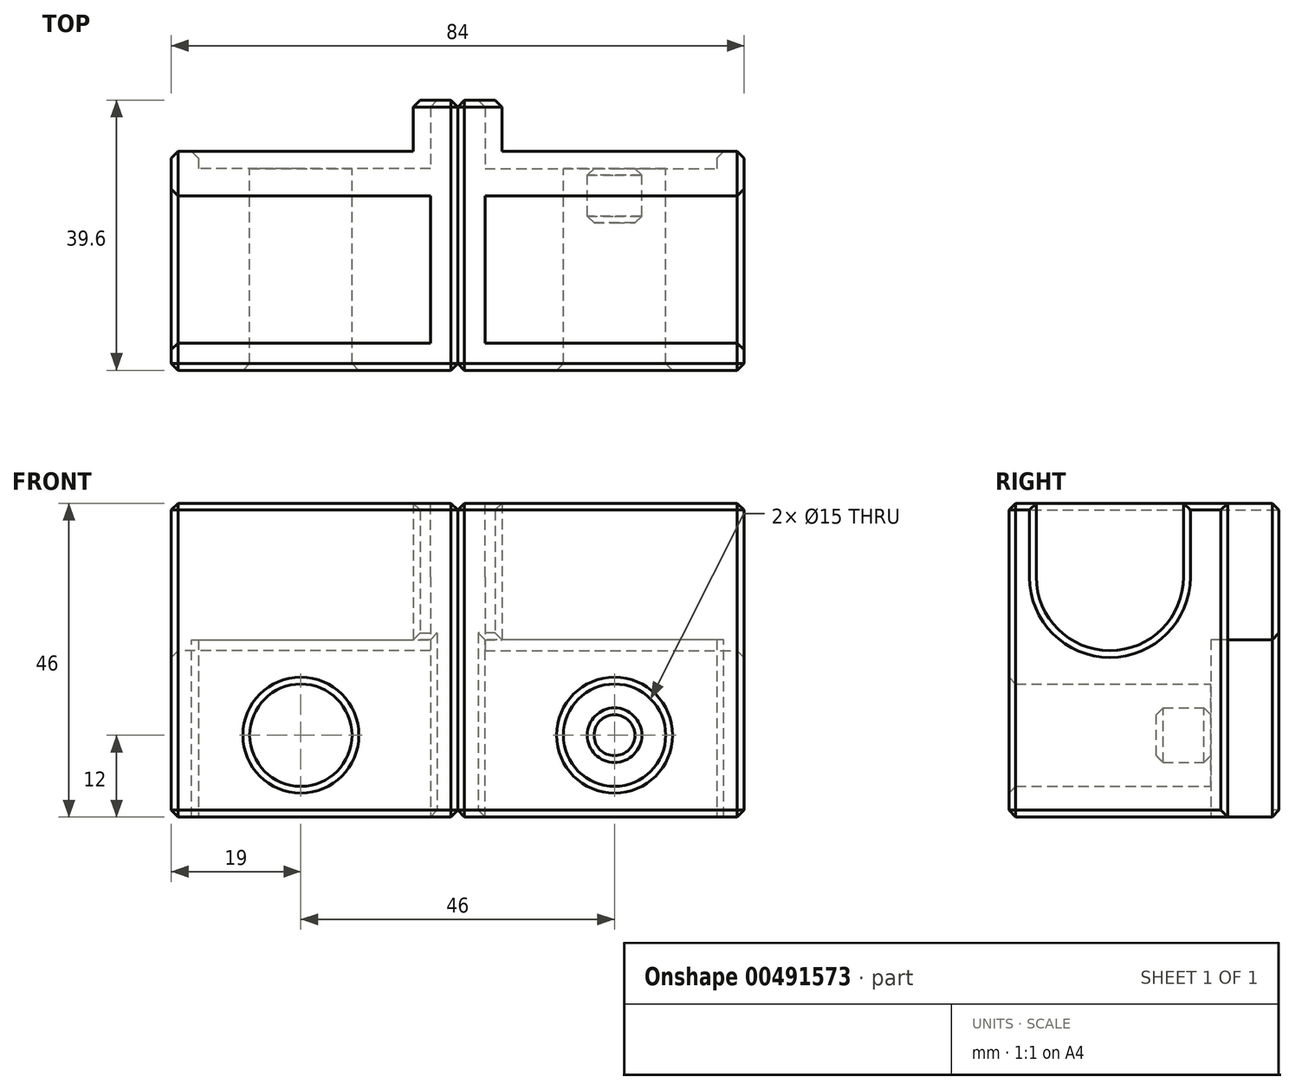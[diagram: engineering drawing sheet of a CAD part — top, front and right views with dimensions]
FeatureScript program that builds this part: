
annotation { "Feature Type Name" : "Feature", "Feature Type Description" : "" }
export const myFeature = defineFeature(function(context is Context, id is Id, definition is map)
    precondition{}
    {
        {
            assignVariable(context, id + "F0", {"name" : "majorEdge", "anyValue" : 19});
        }
        {
            assignVariable(context, id + "F1", {"name" : "minorEdge", "anyValue" : 15});
        }
        {
            assignVariable(context, id + "F2", {"name" : "thickness", "anyValue" : 4});
        }
        {
            assignVariable(context, id + "F3", {"name" : "axleOD", "anyValue" : 21.6});
        }
        {
            assignVariable(context, id + "F4", {"name" : "majorLipDepth", "anyValue" : 10});
        }
        {
            assignVariable(context, id + "F5", {"name" : "minorLipDepth", "anyValue" : 2.5});
        }
        {
            var Q0;
            Q0=qCreatedBy(makeId("Front.planeOp"),FACE);
            var sketch = newSketch(context, id + "F6", { "sketchPlane" : qUnion([Q0])});
            skCircle(sketch, "E0", {"center": v(0, 0) * mm, "radius": 4 * mm});
            skLineSegment(sketch, "E1", {"start": v(0, 4) * mm, "end": v(0, 8) * mm, "construction": true});
            skLineSegment(sketch, "E2", {"start": v(0, 8) * mm, "end": v(-19, 8) * mm});
            skLineSegment(sketch, "E3", {"start": v(-19, 8) * mm, "end": v(-23, 8) * mm});
            skLineSegment(sketch, "E4", {"start": v(0, 8) * mm, "end": v(15, 8) * mm});
            skLineSegment(sketch, "E5", {"start": v(15, 8) * mm, "end": v(19, 8) * mm});
            skLineSegment(sketch, "E6", {"start": v(0, 0) * mm, "end": v(0, -13) * mm, "construction": true});
            skLineSegment(sketch, "E7", {"start": v(0, -13) * mm, "end": v(19, -13) * mm, "construction": true});
            skCircle(sketch, "E8.MirrorC", {"center": v(0, -26) * mm, "radius": 4 * mm});
            skLineSegment(sketch, "E9.MirrorCS", {"start": v(0, -34) * mm, "end": v(15, -34) * mm});
            skLineSegment(sketch, "E10.MirrorCS", {"start": v(0, -34) * mm, "end": v(-19, -34) * mm});
            skLineSegment(sketch, "E11.MirrorCS", {"start": v(-19, -34) * mm, "end": v(-23, -34) * mm});
            skLineSegment(sketch, "E12.MirrorCS", {"start": v(15, -34) * mm, "end": v(19, -34) * mm});
            skLineSegment(sketch, "E13", {"start": v(-23, 8) * mm, "end": v(-23, -34) * mm});
            skLineSegment(sketch, "E14", {"start": v(-19, 8) * mm, "end": v(-19, -34) * mm});
            skLineSegment(sketch, "E15", {"start": v(15, 8) * mm, "end": v(15, -34) * mm});
            skLineSegment(sketch, "E16", {"start": v(19, 8) * mm, "end": v(19, -34) * mm});
            skLineSegment(sketch, "E17", {"start": v(0, -26) * mm, "end": v(0, -12) * mm, "construction": true});
            skLineSegment(sketch, "E18", {"start": v(0, -12) * mm, "end": v(15, -12) * mm});
            skPoint(sketch, "E18.endSnap0", {"position": v(15, -13) * mm});
            skLineSegment(sketch, "E19", {"start": v(0, -12) * mm, "end": v(-19, -12) * mm});
            skCircle(sketch, "E20", {"center": v(0, -26) * mm, "radius": 7.5 * mm});
            skLineSegment(sketch, "E21", {"start": v(-23, -34) * mm, "end": v(-23, -38) * mm});
            skLineSegment(sketch, "E22", {"start": v(-23, -38) * mm, "end": v(19, -38) * mm});
            skLineSegment(sketch, "E23", {"start": v(19, -38) * mm, "end": v(19, -34) * mm});
            skLineSegment(sketch, "E24", {"start": v(15, -34) * mm, "end": v(15, -38) * mm});
            skLineSegment(sketch, "E25", {"start": v(-19, -34) * mm, "end": v(-19, -38) * mm});
            skSolve(sketch);
        }
        {
            var Q0;
            Q0=makeQuery(id+"F6.imprint","IMPRINT",FACE,{"disambiguationData":[TD([[makeQuery(id+"F6.imprint","IMPRINT",EDGE,{"derivedFrom":sQuery(id+"F6.wireOp",EDGE,"E0")}),-1.0]])]});
            var Q1;
            Q1=makeQuery(id+"F6.imprint","IMPRINT",FACE,{"disambiguationData":[TD([[makeQuery(id+"F6.imprint","IMPRINT",EDGE,{"derivedFrom":sQuery(id+"F6.wireOp",EDGE,"E3")}),1.0]])]});
            var Q2;
            Q2=makeQuery(id+"F6.imprint","IMPRINT",FACE,{"disambiguationData":[TD([[makeQuery(id+"F6.imprint","IMPRINT",EDGE,{"derivedFrom":sQuery(id+"F6.wireOp",EDGE,"E5")}),-1.0]])]});
            var Q3;
            Q3=makeQuery(id+"F6.imprint","IMPRINT",FACE,{"disambiguationData":[TD([[makeQuery(id+"F6.imprint","IMPRINT",EDGE,{"derivedFrom":sQuery(id+"F6.wireOp",EDGE,"E0")}),1.0]])]});
            var Q4;
            Q4=makeQuery(id+"F6.imprint","IMPRINT",FACE,{"disambiguationData":[TD([[makeQuery(id+"F6.imprint","IMPRINT",EDGE,{"derivedFrom":sQuery(id+"F6.wireOp",EDGE,"E8.MirrorC")}),1.0]])]});
            var Q5;
            {var subQ1=sQuery(id+"F6.wireOp",EDGE,"E9.MirrorCS");Q5=makeQuery(id+"F6.imprint","IMPRINT",FACE,{"disambiguationData":[TD([[makeQuery(id+"F6.imprint","IMPRINT",EDGE,{"derivedFrom":subQ1}),1.0]])]});}
            var Q6;
            Q6=makeQuery(id+"F6.imprint","IMPRINT",FACE,{"disambiguationData":[TD([[makeQuery(id+"F6.imprint","IMPRINT",EDGE,{"derivedFrom":sQuery(id+"F6.wireOp",EDGE,"E9.MirrorCS")}),-1.0]])]});
            var Q7;
            Q7=makeQuery(id+"F6.imprint","IMPRINT",FACE,{"disambiguationData":[TD([[makeQuery(id+"F6.imprint","IMPRINT",EDGE,{"derivedFrom":sQuery(id+"F6.wireOp",EDGE,"E11.MirrorCS")}),1.0]])]});
            var Q8;
            Q8=makeQuery(id+"F6.imprint","IMPRINT",FACE,{"disambiguationData":[TD([[makeQuery(id+"F6.imprint","IMPRINT",EDGE,{"derivedFrom":sQuery(id+"F6.wireOp",EDGE,"E12.MirrorCS")}),-1.0]])]});
            extrude(context, id + "F7", {"entities" : qUnion([Q0, Q1, Q2, Q3, Q4, Q5, Q6, Q7, Q8]), "depth" : (getVariable(context, 'axleOD') + getVariable(context, 'thickness') * 2) * mm, "offsetDistance" : 25 * mm});
        }
        {
            var Q0;
            Q0=makeQuery(id+"F6.imprint","IMPRINT",FACE,{"disambiguationData":[TD([[makeQuery(id+"F6.imprint","IMPRINT",EDGE,{"derivedFrom":sQuery(id+"F6.wireOp",EDGE,"E0")}),-1.0]])]});
            var Q1;
            Q1=makeQuery(id+"F6.imprint","IMPRINT",FACE,{"disambiguationData":[TD([[makeQuery(id+"F6.imprint","IMPRINT",EDGE,{"derivedFrom":sQuery(id+"F6.wireOp",EDGE,"E0")}),1.0]])]});
            extrude(context, id + "F8", {"entities" : qUnion([Q0, Q1]), "operationType" : NewBodyOperationType.ADD, "oppositeDirection" : true, "depth" : (getVariable(context, 'minorLipDepth')) * mm, "offsetDistance" : 25 * mm});
        }
        {
            var Q0;
            Q0=makeQuery(id+"F6.imprint","IMPRINT",FACE,{"disambiguationData":[TD([[makeQuery(id+"F6.imprint","IMPRINT",EDGE,{"derivedFrom":sQuery(id+"F6.wireOp",EDGE,"E3")}),1.0]])]});
            var Q1;
            Q1=makeQuery(id+"F6.imprint","IMPRINT",FACE,{"disambiguationData":[TD([[makeQuery(id+"F6.imprint","IMPRINT",EDGE,{"derivedFrom":sQuery(id+"F6.wireOp",EDGE,"E11.MirrorCS")}),1.0]])]});
            extrude(context, id + "F9", {"entities" : qUnion([Q0, Q1]), "operationType" : NewBodyOperationType.ADD, "oppositeDirection" : true, "depth" : (getVariable(context, 'majorLipDepth')) * mm, "offsetDistance" : 25 * mm});
        }
        {
            var Q0;
            Q0=makeQuery(id+"F6.imprint","IMPRINT",FACE,{"disambiguationData":[TD([[makeQuery(id+"F6.imprint","IMPRINT",EDGE,{"derivedFrom":sQuery(id+"F6.wireOp",EDGE,"E5")}),-1.0]])]});
            var Q1;
            Q1=makeQuery(id+"F6.imprint","IMPRINT",FACE,{"disambiguationData":[TD([[makeQuery(id+"F6.imprint","IMPRINT",EDGE,{"derivedFrom":sQuery(id+"F6.wireOp",EDGE,"E12.MirrorCS")}),-1.0]])]});
            extrude(context, id + "F10", {"entities" : qUnion([Q0, Q1]), "oppositeDirection" : true, "depth" : (getVariable(context, 'minorLipDepth')) * mm, "offsetDistance" : 25 * mm});
        }
        {
            var Q0;
            Q0=makeQuery(id+"F7.opExtrude","SWEPT_FACE",FACE,{"disambiguationData":[OSD([sQuery(id+"F6.wireOp",EDGE,"E16")])]});
            var sketch = newSketch(context, id + "F11", { "sketchPlane" : qUnion([Q0])});
            skLineSegment(sketch, "E26.0", {"start": v(-29.6, 8) * mm, "end": v(0, 8) * mm, "construction": true});
            skLineSegment(sketch, "E27", {"start": v(-14.8, 8) * mm, "end": v(-14.8, -2.8) * mm, "construction": true});
            skArc(sketch, "E28", {"start": v(-25.6, -2.8) * mm, "mid": v(-14.8, -13.6) * mm, "end": v(-4, -2.8) * mm});
            skLineSegment(sketch, "E29", {"start": v(-25.6, -2.8) * mm, "end": v(-25.6, 8) * mm});
            skLineSegment(sketch, "E30", {"start": v(-4, -2.8) * mm, "end": v(-4, 8) * mm});
            skSolve(sketch);
        }
        {
            var Q0;
            Q0=makeQuery(id+"F11.imprint","IMPRINT",FACE,{"disambiguationData":[TD([[makeQuery(id+"F11.imprint","IMPRINT",EDGE,{"derivedFrom":sQuery(id+"F11.wireOp",EDGE,"E28")}),1.0]])]});
            extrude(context, id + "F12", {"entities" : qUnion([Q0]), "operationType" : NewBodyOperationType.REMOVE, "oppositeDirection" : true, "depth" : (getVariable(context, 'majorEdge') + getVariable(context, 'minorEdge') + getVariable(context, 'thickness')) * mm, "offsetDistance" : 25 * mm});
        }
        {
            var Q0;
            Q0=makeQuery(id+"F10.opExtrude","SWEPT_BODY",BODY,{"disambiguationData":[OSD([sQuery(id+"F6.wireOp",EDGE,"E5"),sQuery(id+"F6.wireOp",EDGE,"E12.MirrorCS"),sQuery(id+"F6.wireOp",EDGE,"E15"),sQuery(id+"F6.wireOp",EDGE,"E16")])]});
            var Q1;
            Q1=makeQuery(id+"F7.opExtrude","SWEPT_BODY",BODY,{"disambiguationData":[OSD([sQuery(id+"F6.wireOp",EDGE,"E2"),sQuery(id+"F6.wireOp",EDGE,"E3"),sQuery(id+"F6.wireOp",EDGE,"E4"),sQuery(id+"F6.wireOp",EDGE,"E5"),sQuery(id+"F6.wireOp",EDGE,"E8.MirrorC"),sQuery(id+"F6.wireOp",EDGE,"E9.MirrorCS"),sQuery(id+"F6.wireOp",EDGE,"E10.MirrorCS"),sQuery(id+"F6.wireOp",EDGE,"E11.MirrorCS"),sQuery(id+"F6.wireOp",EDGE,"E12.MirrorCS"),sQuery(id+"F6.wireOp",EDGE,"E13"),sQuery(id+"F6.wireOp",EDGE,"E16")])]});
            booleanBodies(context, id + "F13", {"operationType" : BooleanOperationType.UNION, "tools" : qUnion([Q0, Q1])});
        }
        {
            var Q0;
            Q0=makeQuery(id+"F9.opExtrude","SWEPT_FACE",FACE,{"disambiguationData":[OSD([sQuery(id+"F6.wireOp",EDGE,"E14")])]});
            var sketch = newSketch(context, id + "F14", { "sketchPlane" : qUnion([Q0])});
            skLineSegment(sketch, "E31.0", {"start": v(2.5, 8) * mm, "end": v(2.5, -12) * mm});
            skLineSegment(sketch, "E32.0", {"start": v(10, 8) * mm, "end": v(2.5, 8) * mm});
            skLineSegment(sketch, "E33", {"start": v(2.5, -12) * mm, "end": v(10, -12) * mm});
            skLineSegment(sketch, "E34", {"start": v(10, -12) * mm, "end": v(10, 8) * mm});
            skSolve(sketch);
        }
        {
            var Q0;
            Q0=makeQuery(id+"F14.imprint","IMPRINT",FACE,{"disambiguationData":[TD([[makeQuery(id+"F14.imprint","IMPRINT",EDGE,{"derivedFrom":sQuery(id+"F14.wireOp",EDGE,"E31.0")}),1.0]])]});
            extrude(context, id + "F15", {"entities" : qUnion([Q0]), "operationType" : NewBodyOperationType.ADD, "depth" : (getVariable(context, 'minorLipDepth')) * mm, "offsetDistance" : 25 * mm});
        }
        {
            var Q0;
            Q0=makeQuery(id+"F7.opExtrude","CAP_FACE",FACE,{"disambiguationData":[OSD([sQuery(id+"F6.wireOp",EDGE,"E2"),sQuery(id+"F6.wireOp",EDGE,"E3"),sQuery(id+"F6.wireOp",EDGE,"E4"),sQuery(id+"F6.wireOp",EDGE,"E5"),sQuery(id+"F6.wireOp",EDGE,"E8.MirrorC"),sQuery(id+"F6.wireOp",EDGE,"E13"),sQuery(id+"F6.wireOp",EDGE,"E16"),sQuery(id+"F6.wireOp",EDGE,"E21"),sQuery(id+"F6.wireOp",EDGE,"E22"),sQuery(id+"F6.wireOp",EDGE,"E23")])],"isStart":false});
            var sketch = newSketch(context, id + "F16", { "sketchPlane" : qUnion([Q0])});
            skCircle(sketch, "E35.1", {"center": v(0, -26) * mm, "radius": 7.5 * mm});
            skSolve(sketch);
        }
        {
            var Q0;
            Q0=makeQuery(id+"F16.imprint","IMPRINT",FACE,{"disambiguationData":[TD([[makeQuery(id+"F16.imprint","IMPRINT",EDGE,{"derivedFrom":sQuery(id+"F16.wireOp",EDGE,"E35.1")}),1.0]])]});
            var Q1;
            Q1=makeQuery(id+"F16.imprint","IMPRINT",FACE,{"disambiguationData":[TD([[makeQuery(id+"F16.imprint","IMPRINT",EDGE,{"derivedFrom":makeQuery(id+"F7.opExtrude","CAP_EDGE",EDGE,{"disambiguationData":[OSD([sQuery(id+"F6.wireOp",EDGE,"E8.MirrorC")])],"isStart":false})}),-1.0]])]});
            var Q2;
            Q2=sQuery(id+"F16.wireOp",EDGE,"E35.1");
            extrude(context, id + "F17", {"entities" : qUnion([Q0, Q1]), "operationType" : NewBodyOperationType.REMOVE, "surfaceEntities" : qUnion([Q2]), "oppositeDirection" : true, "depth" : (getVariable(context, 'axleOD')) * mm, "offsetDistance" : 25 * mm});
        }
        {
            var Q0;
            Q0=makeQuery(id+"F7.opExtrude","CAP_EDGE",EDGE,{"disambiguationData":[OSD([sQuery(id+"F6.wireOp",EDGE,"E8.MirrorC")])],"isStart":false});
            var Q1;
            Q1=makeQuery(id+"F7.opExtrude","CAP_EDGE",EDGE,{"disambiguationData":[OSD([sQuery(id+"F6.wireOp",EDGE,"E8.MirrorC")])],"isStart":true});
            var Q2;
            {var subQ0=sQuery(id+"F6.wireOp",EDGE,"E13");Q2=makeQuery(id+"F9.boolean.opBoolean","MERGE",FACE,{"derivedFrom":[makeQuery(id+"F7.opExtrude","SWEPT_FACE",FACE,{"disambiguationData":[OSD([subQ0])]}),makeQuery(id+"F9.opExtrude","SWEPT_FACE",FACE,{"disambiguationData":[OSD([subQ0])]})]});}
            var Q3;
            Q3=makeQuery(id+"F7.opExtrude","CAP_FACE",FACE,{"disambiguationData":[OSD([sQuery(id+"F6.wireOp",EDGE,"E2"),sQuery(id+"F6.wireOp",EDGE,"E3"),sQuery(id+"F6.wireOp",EDGE,"E4"),sQuery(id+"F6.wireOp",EDGE,"E5"),sQuery(id+"F6.wireOp",EDGE,"E8.MirrorC"),sQuery(id+"F6.wireOp",EDGE,"E9.MirrorCS"),sQuery(id+"F6.wireOp",EDGE,"E10.MirrorCS"),sQuery(id+"F6.wireOp",EDGE,"E11.MirrorCS"),sQuery(id+"F6.wireOp",EDGE,"E12.MirrorCS"),sQuery(id+"F6.wireOp",EDGE,"E13"),sQuery(id+"F6.wireOp",EDGE,"E16")])],"isStart":false});
            var Q4;
            {var subQ0=sQuery(id+"F6.wireOp",EDGE,"E16");Q4=makeQuery(id+"F13.opBoolean","MERGE",FACE,{"derivedFrom":[makeQuery(id+"F10.opExtrude","SWEPT_FACE",FACE,{"disambiguationData":[OSD([subQ0])]}),makeQuery(id+"F7.opExtrude","SWEPT_FACE",FACE,{"disambiguationData":[OSD([subQ0])]})]});}
            var Q5;
            Q5=makeQuery(id+"F9.opExtrude","CAP_FACE",FACE,{"disambiguationData":[OSD([sQuery(id+"F6.wireOp",EDGE,"E3"),sQuery(id+"F6.wireOp",EDGE,"E11.MirrorCS"),sQuery(id+"F6.wireOp",EDGE,"E13"),sQuery(id+"F6.wireOp",EDGE,"E14")])],"isStart":false});
            var Q6;
            Q6=makeQuery(id+"F12.boolean.opBoolean","COPY",EDGE,{"derivedFrom":makeQuery(id+"F12.opExtrude","SWEPT_EDGE",EDGE,{"disambiguationData":[OSD([sQuery(id+"F6.wireOp",EDGE,"E5"),sQuery(id+"F6.wireOp",EDGE,"E16"),sQuery(id+"F11.wireOp",EDGE,"E30")])]})});
            var Q7;
            Q7=makeQuery(id+"F12.boolean.opBoolean","COPY",EDGE,{"derivedFrom":makeQuery(id+"F12.opExtrude","CAP_EDGE",EDGE,{"disambiguationData":[OSD([sQuery(id+"F6.wireOp",EDGE,"E5"),sQuery(id+"F6.wireOp",EDGE,"E16")])],"isStart":false})});
            var Q8;
            Q8=makeQuery(id+"F12.boolean.opBoolean","COPY",EDGE,{"derivedFrom":makeQuery(id+"F12.opExtrude","SWEPT_EDGE",EDGE,{"disambiguationData":[OSD([sQuery(id+"F6.wireOp",EDGE,"E5"),sQuery(id+"F6.wireOp",EDGE,"E16"),sQuery(id+"F11.wireOp",EDGE,"E29")])]})});
            var Q9;
            Q9=makeQuery(id+"F10.opExtrude","CAP_EDGE",EDGE,{"disambiguationData":[OSD([sQuery(id+"F6.wireOp",EDGE,"E15")])],"isStart":false});
            var Q10;
            Q10=makeQuery(id+"F17.boolean.opBoolean","INTERSECT",EDGE,{"derivedFrom":[makeQuery(id+"F7.opExtrude","SWEPT_FACE",FACE,{"disambiguationData":[OSD([sQuery(id+"F6.wireOp",EDGE,"E8.MirrorC")])]}),makeQuery(id+"F17.opExtrude","CAP_FACE",FACE,{"disambiguationData":[OSD([sQuery(id+"F16.wireOp",EDGE,"E35.1")])],"isStart":false})]});
            chamfer(context, id + "F18", {"entities" : qUnion([Q0, Q1, Q2, Q3, Q4, Q5, Q6, Q7, Q8, Q9, Q10]), "width" : 1 * mm, "tangentPropagation" : true});
        }
        {
            var Q0;
            Q0=makeQuery(id+"F10.opExtrude","SWEPT_BODY",BODY,{"disambiguationData":[OSD([sQuery(id+"F6.wireOp",EDGE,"E5"),sQuery(id+"F6.wireOp",EDGE,"E15"),sQuery(id+"F6.wireOp",EDGE,"E16"),sQuery(id+"F6.wireOp",EDGE,"E22"),sQuery(id+"F6.wireOp",EDGE,"E23"),sQuery(id+"F6.wireOp",EDGE,"E24")])]});
            var Q1;
            {var subQ0=sQuery(id+"F6.wireOp",EDGE,"E21");var subQ1=sQuery(id+"F6.wireOp",EDGE,"E13");Q1=makeQuery(id+"F9.boolean.opBoolean","MERGE",FACE,{"derivedFrom":[makeQuery(id+"F7.opExtrude","SWEPT_FACE",FACE,{"disambiguationData":[OSD([subQ1,subQ0])]}),makeQuery(id+"F9.opExtrude","SWEPT_FACE",FACE,{"disambiguationData":[OSD([subQ1,subQ0])]})]});}
            mirror(context, id + "F19", {"entities" : qUnion([Q0]), "mirrorPlane" : qUnion([Q1])});
        }
    });
